# Revit family: TYCO-FPP-FireClass-FC410CIM CONTACT IP MODULE
name_source: partatom
category: Electrical Fixtures
revit_build: Autodesk Revit 2014 (Build: 20130308_1515(x64)
units: mm (PartAtom-declared; Revit-internal decimal feet)

## types (1)
- TYCO-FPP-FireClass-FC410CIM CONTACT IP MODULE
    Alarm State Current = 2.8mA
    Description = Contact Module FC410CIM
    EOL Resistor = 200 Ohm
    Front Cover = Yes
    Keynote = Two spur circuits monitoring multiple normally open contacts,
with short circuit giving a fault output.
    Length = 61 mm
    Loop Voltage = 20V to 40Vdc
    Manufacturer = Tyco
    Model = FireClass - 555.800.702
    Monitor Resistor Value = 100 Ohm
    Operating Temperature = - 25 - + 70 ºC
    PCB = PCB
    Rear Cover = Yes
    Relative Humidity = 10% to 95%
    Storage Temperature = –40°C to +80°C
    Type Comments = The FC410CIM FC Addressable Contact Input Module is designed to monitor
fire contacts such as extinguishing system control, ventilation control, fire
door control etc
    URL = https://fireclass.co.uk
    Width = 84 mm
    Wire Size (maximum) = 2.5sq. mm

## geometry (parser evidence)
native form markers: Sweep x5
no freeform markers — native parametric forms only
